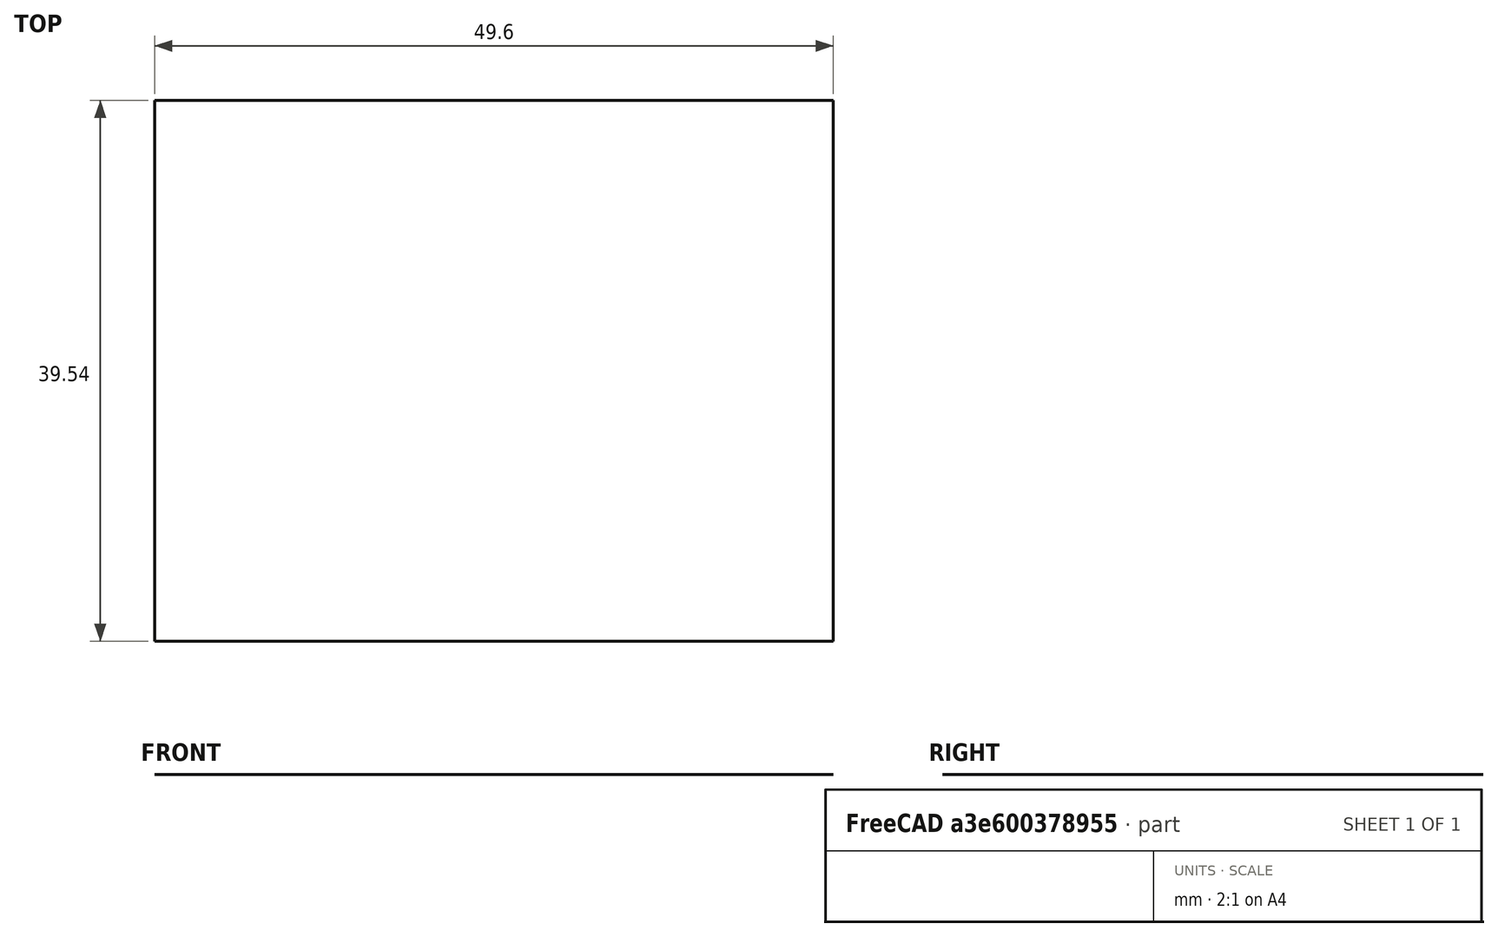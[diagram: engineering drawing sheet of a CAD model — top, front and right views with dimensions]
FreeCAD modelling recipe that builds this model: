
FCSTD DOCUMENT  (FreeCAD 0.16R6712 (Git))
Label: plane
License: All rights reserved
LicenseURL: http://en.wikipedia.org/wiki/All_rights_reserved
objects: Sketcher::SketchObject×1, Part::RuledSurface×1, Mesh::Feature×1
note: 2 computed .brp shape members not serialized (recipe doc carries the construction recipe); baked Part::Feature solids carry a one-line shape summary decoded from their .brp

FEATURE [Sketcher::SketchObject] Sketch
  sketch-geometry (4):
    g0: LineSegment StartX=-29.4029 StartY=19.7724 StartZ=0 EndX=20.1985 EndY=19.7724 EndZ=0
    g1: LineSegment StartX=20.1985 StartY=19.7724 StartZ=0 EndX=20.1985 EndY=-19.7724 EndZ=0
    g2: LineSegment StartX=20.1985 StartY=-19.7724 StartZ=0 EndX=-29.4029 EndY=-19.7724 EndZ=0
    g3: LineSegment StartX=-29.4029 StartY=-19.7724 StartZ=0 EndX=-29.4029 EndY=19.7724 EndZ=0
  constraints (8):
    c: Coincident(g0,g1)
    c: Coincident(g1,g2)
    c: Coincident(g2,g3)
    c: Coincident(g3,g0)
    c: Horizontal(g0)
    c: Horizontal(g2)
    c: Vertical(g1)
    c: Vertical(g3)
FEATURE [Part::RuledSurface] Ruled_Surface
  Curve1 = -> Sketch [Edge3]
  Curve2 = -> Sketch [Edge1]
  Orientation = 0
FEATURE [Mesh::Feature] Mesh  label="Ruled_Surface (Meshed)"
